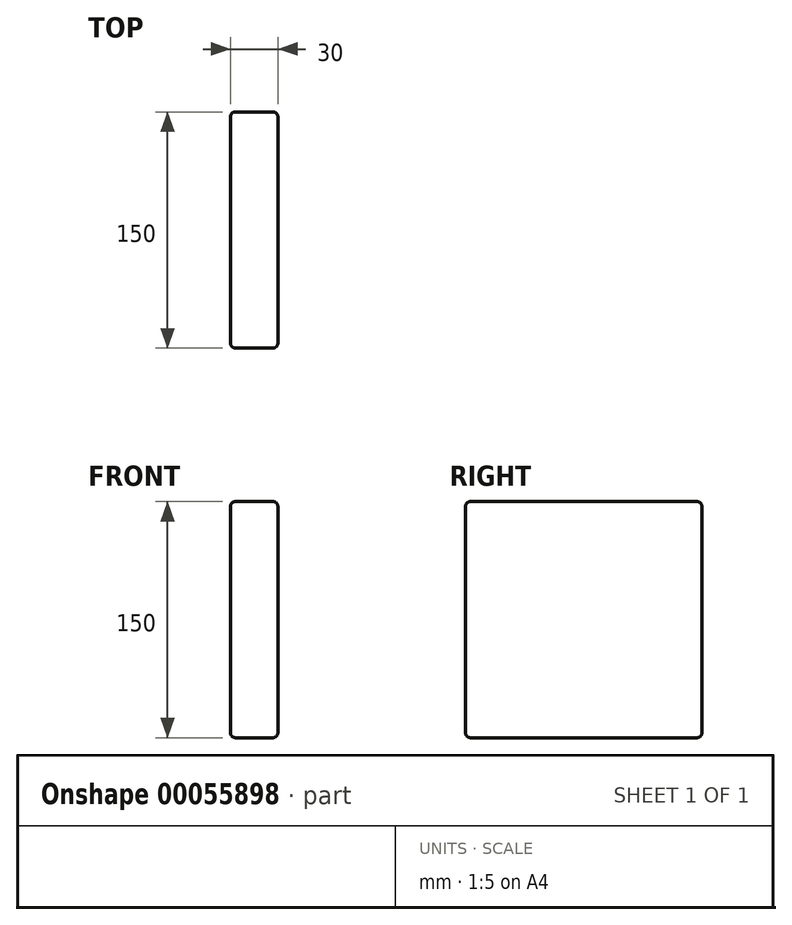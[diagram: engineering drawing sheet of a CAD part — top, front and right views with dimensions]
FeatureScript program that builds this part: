
annotation { "Feature Type Name" : "Feature", "Feature Type Description" : "" }
export const myFeature = defineFeature(function(context is Context, id is Id, definition is map)
    precondition{}
    {
        {
            var Q0;
            Q0=qCreatedBy(makeId("Right.planeOp"),FACE);
            var sketch = newSketch(context, id + "F0", { "sketchPlane" : qUnion([Q0])});
            skLineSegment(sketch, "E0.bottom", {"start": v(-81.37, 76.22) * mm, "end": v(68.63, 76.22) * mm});
            skLineSegment(sketch, "E0.top", {"start": v(-81.37, -73.78) * mm, "end": v(68.63, -73.78) * mm});
            skLineSegment(sketch, "E0.left", {"start": v(-81.37, 76.22) * mm, "end": v(-81.37, -73.78) * mm});
            skLineSegment(sketch, "E0.right", {"start": v(68.63, 76.22) * mm, "end": v(68.63, -73.78) * mm});
            skSolve(sketch);
        }
        {
            var Q0;
            Q0 = qSketchRegion(id + "F0", true);
            extrude(context, id + "F1", {"entities" : qUnion([Q0]), "depth" : 30 * mm});
        }
        {
            var Q0;
            Q0=makeQuery(id+"F1.opExtrude","CAP_EDGE",EDGE,{"disambiguationData":[OSD([sQuery(id+"F0.wireOp",EDGE,"E0.bottom")])],"isStart":false});
            var Q1;
            Q1=makeQuery(id+"F1.opExtrude","SWEPT_EDGE",EDGE,{"disambiguationData":[OSD([sQuery(id+"F0.wireOp",EDGE,"E0.bottom"),sQuery(id+"F0.wireOp",EDGE,"E0.left")])]});
            var Q2;
            Q2=makeQuery(id+"F1.opExtrude","CAP_EDGE",EDGE,{"disambiguationData":[OSD([sQuery(id+"F0.wireOp",EDGE,"E0.bottom")])],"isStart":true});
            var Q3;
            Q3=makeQuery(id+"F1.opExtrude","SWEPT_EDGE",EDGE,{"disambiguationData":[OSD([sQuery(id+"F0.wireOp",EDGE,"E0.bottom"),sQuery(id+"F0.wireOp",EDGE,"E0.right")])]});
            var Q4;
            Q4=makeQuery(id+"F1.opExtrude","CAP_EDGE",EDGE,{"disambiguationData":[OSD([sQuery(id+"F0.wireOp",EDGE,"E0.left")])],"isStart":false});
            var Q5;
            Q5=makeQuery(id+"F1.opExtrude","CAP_EDGE",EDGE,{"disambiguationData":[OSD([sQuery(id+"F0.wireOp",EDGE,"E0.left")])],"isStart":true});
            var Q6;
            Q6=makeQuery(id+"F1.opExtrude","SWEPT_EDGE",EDGE,{"disambiguationData":[OSD([sQuery(id+"F0.wireOp",EDGE,"E0.top"),sQuery(id+"F0.wireOp",EDGE,"E0.left")])]});
            var Q7;
            Q7=makeQuery(id+"F1.opExtrude","CAP_EDGE",EDGE,{"disambiguationData":[OSD([sQuery(id+"F0.wireOp",EDGE,"E0.top")])],"isStart":false});
            var Q8;
            Q8=makeQuery(id+"F1.opExtrude","CAP_EDGE",EDGE,{"disambiguationData":[OSD([sQuery(id+"F0.wireOp",EDGE,"E0.right")])],"isStart":false});
            var Q9;
            Q9=makeQuery(id+"F1.opExtrude","CAP_EDGE",EDGE,{"disambiguationData":[OSD([sQuery(id+"F0.wireOp",EDGE,"E0.right")])],"isStart":true});
            var Q10;
            Q10=makeQuery(id+"F1.opExtrude","SWEPT_EDGE",EDGE,{"disambiguationData":[OSD([sQuery(id+"F0.wireOp",EDGE,"E0.top"),sQuery(id+"F0.wireOp",EDGE,"E0.right")])]});
            var Q11;
            Q11=makeQuery(id+"F1.opExtrude","CAP_EDGE",EDGE,{"disambiguationData":[OSD([sQuery(id+"F0.wireOp",EDGE,"E0.top")])],"isStart":true});
            fillet(context, id + "F2", {"entities" : qUnion([Q0, Q1, Q2, Q3, Q4, Q5, Q6, Q7, Q8, Q9, Q10, Q11]), "radius" : 3 * mm, "tangentPropagation" : true, "allowEdgeOverflow" : false});
        }
    });
